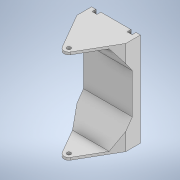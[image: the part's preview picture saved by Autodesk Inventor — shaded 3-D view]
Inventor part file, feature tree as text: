
AUTODESK INVENTOR PART (.ipt)
format: ipt  version: 2020 (Build 240168000, 168)  size: 146,944 bytes
history: native  units: in
note: dims shown in document units (in); Inventor stores cm internally (conversion verified against a paired STEP export)
features: extrude x3, sketch x3
ambient origin geometry x8: Origin, YZ Plane, XZ Plane, XY Plane, X Axis, Y Axis, Z Axis, Center Point
bodies: Solid1 (feature_tree)
feature tree (6):
  extrude  "Extrusion1"  Depth=0.6299in
  extrude  "Extrusion2"  TaperAngle=60.0deg  [1 undecoded]
  extrude  "Extrusion3"  Depth=0.7874in
  sketch  "Sketch1"  dims[d0=0.6299in d2=3.937in]
  sketch  "Sketch2"  dims[d3=3.1496in d4=60.0deg]
  sketch  "Sketch3"  dims[d5=2.3622in d6=0.7874in d7=15.1181in d8=0.0in d9=0.3937in d10=7.0866in d11=4.3307in d12=0.9963in d13=3.937in d14=0.0in d15=0.7087in d16=0.7874in d17=0.6299in d18=0.0in d19=0.0in]
note: 1 required parameter value undecoded (feature->parameter linkage not recoverable at this tier; creation-order binding heuristic only, values carry confidence <= 0.55)
